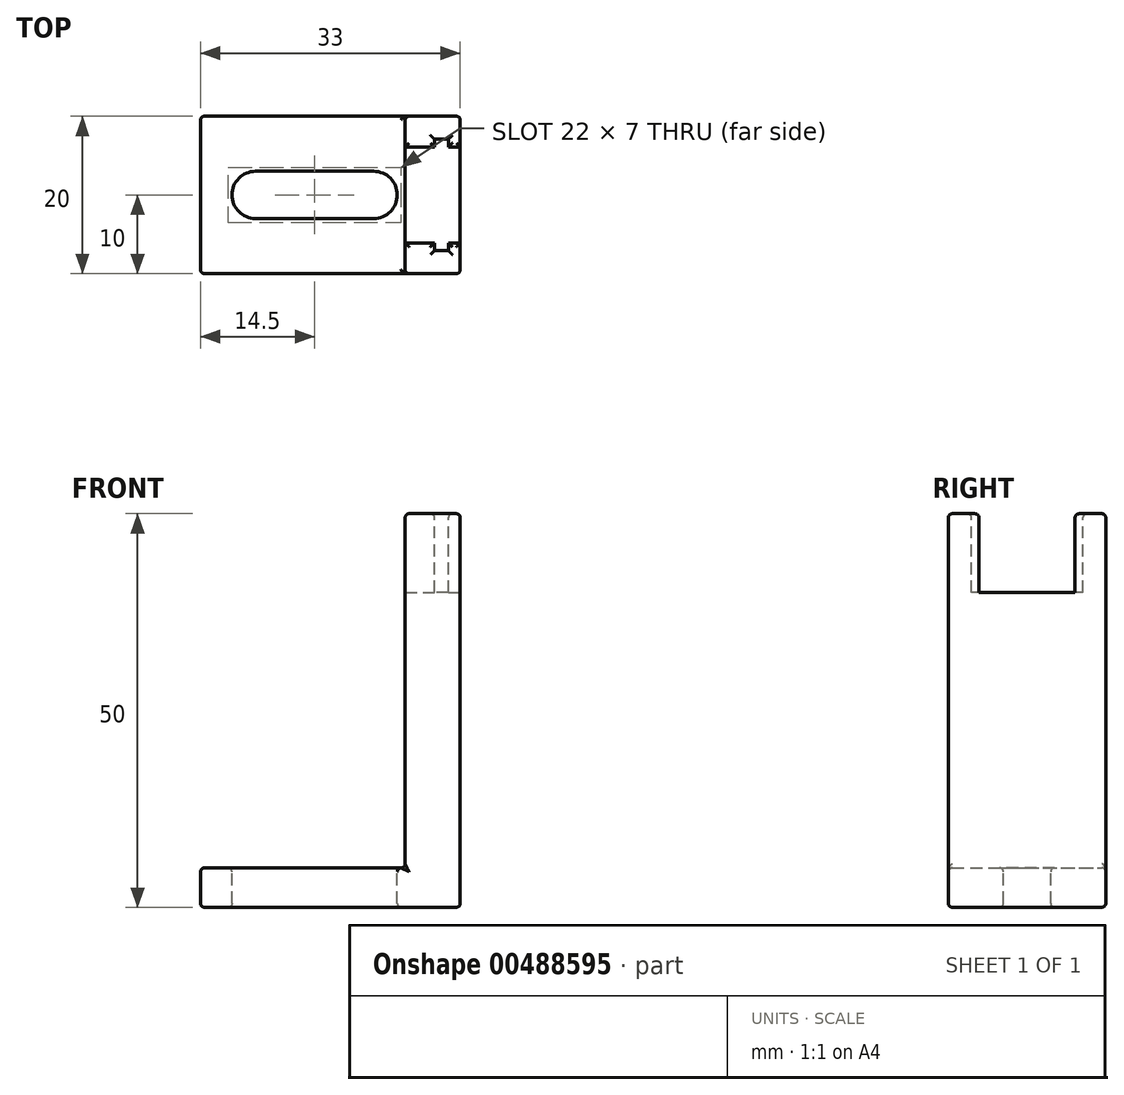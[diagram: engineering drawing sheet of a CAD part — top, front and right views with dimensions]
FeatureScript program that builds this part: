
annotation { "Feature Type Name" : "Feature", "Feature Type Description" : "" }
export const myFeature = defineFeature(function(context is Context, id is Id, definition is map)
    precondition{}
    {
        {
            var Q0;
            Q0=qCreatedBy(makeId("Front.planeOp"),FACE);
            var sketch = newSketch(context, id + "F0", { "sketchPlane" : qUnion([Q0])});
            skLineSegment(sketch, "E0", {"start": v(0, 0) * mm, "end": v(-33, 0) * mm});
            skLineSegment(sketch, "E1", {"start": v(-33, 0) * mm, "end": v(-33, 5) * mm});
            skLineSegment(sketch, "E2", {"start": v(-33, 5) * mm, "end": v(-7, 5) * mm});
            skLineSegment(sketch, "E3", {"start": v(-7, 5) * mm, "end": v(-7, 50) * mm});
            skLineSegment(sketch, "E4", {"start": v(-7, 50) * mm, "end": v(0, 50) * mm});
            skLineSegment(sketch, "E5", {"start": v(0, 50) * mm, "end": v(0, 0) * mm});
            skSolve(sketch);
        }
        {
            var Q0;
            Q0 = qSketchRegion(id + "F0", true);
            extrude(context, id + "F1", {"entities" : qUnion([Q0]), "depth" : 20 * mm});
        }
        {
            var Q0;
            Q0=makeQuery(id+"F1.opExtrude","SWEPT_FACE",FACE,{"disambiguationData":[OSD([sQuery(id+"F0.wireOp",EDGE,"E2")])]});
            var sketch = newSketch(context, id + "F2", { "sketchPlane" : qUnion([Q0])});
            skArc(sketch, "E6", {"start": v(-26, -7) * mm, "mid": v(-29, -10) * mm, "end": v(-26, -13) * mm});
            skLineSegment(sketch, "E7", {"start": v(-26, -7) * mm, "end": v(-11, -7) * mm});
            skLineSegment(sketch, "E8", {"start": v(-26, -13) * mm, "end": v(-11, -13) * mm});
            skArc(sketch, "E9", {"start": v(-11, -13) * mm, "mid": v(-8, -10) * mm, "end": v(-11, -7) * mm});
            skSolve(sketch);
        }
        {
            var Q0;
            Q0 = qSketchRegion(id + "F2", true);
            extrude(context, id + "F3", {"entities" : qUnion([Q0]), "operationType" : NewBodyOperationType.REMOVE, "oppositeDirection" : true, "depth" : 25 * mm});
        }
        {
            var Q0;
            Q0=makeQuery(id+"F1.opExtrude","SWEPT_FACE",FACE,{"disambiguationData":[OSD([sQuery(id+"F0.wireOp",EDGE,"E4")])]});
            var sketch = newSketch(context, id + "F4", { "sketchPlane" : qUnion([Q0])});
            skLineSegment(sketch, "E10.bottom", {"start": v(-1.5, -2.9) * mm, "end": v(-3.3, -2.9) * mm});
            skLineSegment(sketch, "E10.top", {"start": v(-1.5, -17.1) * mm, "end": v(-3.3, -17.1) * mm});
            skLineSegment(sketch, "E10.left", {"start": v(-1.5, -2.9) * mm, "end": v(-1.5, -17.1) * mm});
            skLineSegment(sketch, "E10.right", {"start": v(-3.3, -2.9) * mm, "end": v(-3.3, -17.1) * mm});
            skSolve(sketch);
        }
        {
            var Q0;
            Q0 = qSketchRegion(id + "F4", true);
            extrude(context, id + "F5", {"entities" : qUnion([Q0]), "operationType" : NewBodyOperationType.REMOVE, "oppositeDirection" : true, "depth" : 10 * mm});
        }
        {
            var Q0;
            Q0=makeQuery(id+"F1.opExtrude","CAP_FACE",FACE,{"disambiguationData":[OSD([sQuery(id+"F0.wireOp",EDGE,"E0"),sQuery(id+"F0.wireOp",EDGE,"E1"),sQuery(id+"F0.wireOp",EDGE,"E2"),sQuery(id+"F0.wireOp",EDGE,"E3"),sQuery(id+"F0.wireOp",EDGE,"E4"),sQuery(id+"F0.wireOp",EDGE,"E5")])],"isStart":false});
            fillet(context, id + "F6", {"entities" : qUnion([Q0]), "radius" : 0.5 * mm, "tangentPropagation" : true, "allowEdgeOverflow" : false});
        }
        {
            var Q0;
            Q0=makeQuery(id+"F1.opExtrude","CAP_FACE",FACE,{"disambiguationData":[OSD([sQuery(id+"F0.wireOp",EDGE,"E0"),sQuery(id+"F0.wireOp",EDGE,"E1"),sQuery(id+"F0.wireOp",EDGE,"E2"),sQuery(id+"F0.wireOp",EDGE,"E3"),sQuery(id+"F0.wireOp",EDGE,"E4"),sQuery(id+"F0.wireOp",EDGE,"E5")])],"isStart":true});
            fillet(context, id + "F7", {"entities" : qUnion([Q0]), "radius" : 0.5 * mm, "tangentPropagation" : true, "allowEdgeOverflow" : false});
        }
        {
            var Q0;
            Q0=makeQuery(id+"F1.opExtrude","SWEPT_FACE",FACE,{"disambiguationData":[OSD([sQuery(id+"F0.wireOp",EDGE,"E1")])]});
            fillet(context, id + "F8", {"entities" : qUnion([Q0]), "radius" : 0.5 * mm, "tangentPropagation" : true, "allowEdgeOverflow" : false});
        }
        {
            var Q0;
            Q0=makeQuery(id+"F1.opExtrude","SWEPT_FACE",FACE,{"disambiguationData":[OSD([sQuery(id+"F0.wireOp",EDGE,"E0")])]});
            fillet(context, id + "F9", {"entities" : qUnion([Q0]), "radius" : 0.5 * mm, "tangentPropagation" : true, "allowEdgeOverflow" : false});
        }
        {
            var Q0;
            Q0=makeQuery(id+"F1.opExtrude","SWEPT_FACE",FACE,{"disambiguationData":[OSD([sQuery(id+"F0.wireOp",EDGE,"E2")])]});
            fillet(context, id + "F10", {"entities" : qUnion([Q0]), "radius" : 0.5 * mm, "tangentPropagation" : true, "allowEdgeOverflow" : false});
        }
        {
            var Q0;
            Q0=makeQuery(id+"F1.opExtrude","SWEPT_FACE",FACE,{"disambiguationData":[OSD([sQuery(id+"F0.wireOp",EDGE,"E5")])]});
            var sketch = newSketch(context, id + "F11", { "sketchPlane" : qUnion([Q0])});
            skLineSegment(sketch, "E11.bottom", {"start": v(-16.1, 50) * mm, "end": v(-3.9, 50) * mm});
            skLineSegment(sketch, "E11.top", {"start": v(-16.1, 40) * mm, "end": v(-3.9, 40) * mm});
            skLineSegment(sketch, "E11.left", {"start": v(-16.1, 50) * mm, "end": v(-16.1, 40) * mm});
            skLineSegment(sketch, "E11.right", {"start": v(-3.9, 50) * mm, "end": v(-3.9, 40) * mm});
            skSolve(sketch);
        }
        {
            var Q0;
            Q0 = qSketchRegion(id + "F11", true);
            extrude(context, id + "F12", {"entities" : qUnion([Q0]), "operationType" : NewBodyOperationType.REMOVE, "oppositeDirection" : true, "depth" : 25 * mm});
        }
        {
            var Q0;
            {var subQ1=sQuery(id+"F0.wireOp",EDGE,"E4");Q0=makeQuery(id+"F12.boolean.opBoolean","SPLIT",FACE,{"disambiguationData":[TD([makeQuery(id+"F5.boolean.opBoolean","COPY",FACE,{"derivedFrom":makeQuery(id+"F5.opExtrude","SWEPT_FACE",FACE,{"disambiguationData":[OSD([sQuery(id+"F4.wireOp",EDGE,"E10.top")])]})})])],"derivedFrom":makeQuery(id+"F1.opExtrude","SWEPT_FACE",FACE,{"disambiguationData":[OSD([subQ1])]})});}
            fillet(context, id + "F13", {"entities" : qUnion([Q0]), "radius" : 0.5 * mm, "tangentPropagation" : true, "allowEdgeOverflow" : false});
        }
        {
            var Q0;
            {var subQ2=sQuery(id+"F0.wireOp",EDGE,"E4");Q0=makeQuery(id+"F12.boolean.opBoolean","SPLIT",FACE,{"disambiguationData":[TD([makeQuery(id+"F5.boolean.opBoolean","COPY",FACE,{"derivedFrom":makeQuery(id+"F5.opExtrude","SWEPT_FACE",FACE,{"disambiguationData":[OSD([sQuery(id+"F4.wireOp",EDGE,"E10.bottom")])]})})])],"derivedFrom":makeQuery(id+"F1.opExtrude","SWEPT_FACE",FACE,{"disambiguationData":[OSD([subQ2])]})});}
            fillet(context, id + "F14", {"entities" : qUnion([Q0]), "radius" : 0.5 * mm, "tangentPropagation" : true, "allowEdgeOverflow" : false});
        }
    });
